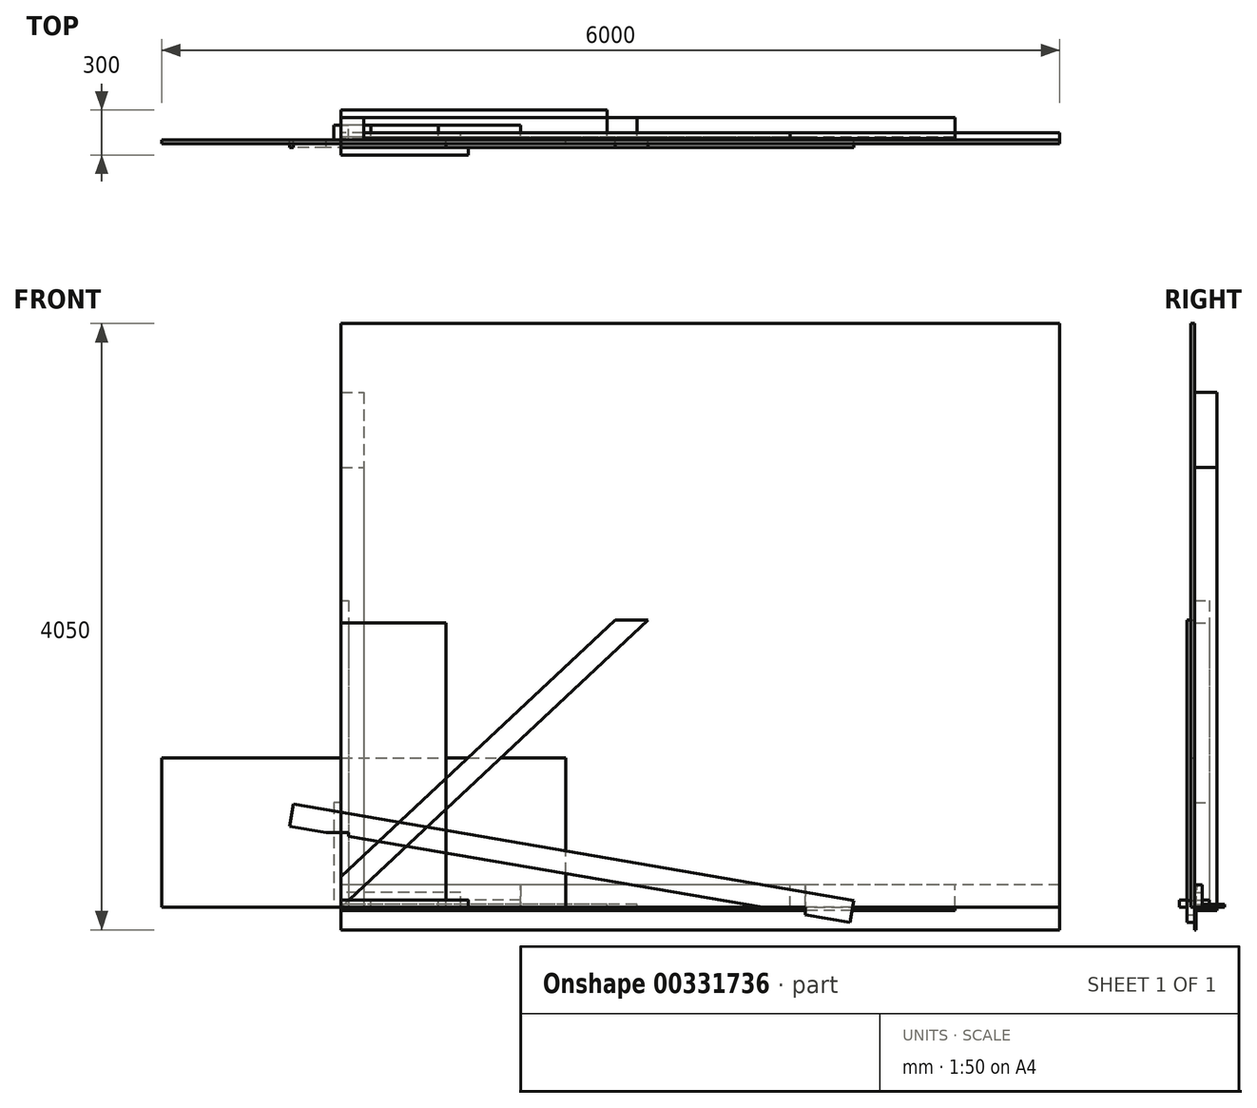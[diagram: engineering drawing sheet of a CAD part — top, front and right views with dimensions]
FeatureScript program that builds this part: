
annotation { "Feature Type Name" : "Feature", "Feature Type Description" : "" }
export const myFeature = defineFeature(function(context is Context, id is Id, definition is map)
    precondition{}
    {
        {
            var Q0;
            Q0=qCreatedBy(makeId("Top.planeOp"),FACE);
            var sketch = newSketch(context, id + "F0", { "sketchPlane" : qUnion([Q0])});
            skLineSegment(sketch, "E0.bottom", {"start": v(0, 0) * mm, "end": v(150, 0) * mm});
            skLineSegment(sketch, "E0.top", {"start": v(0, 150) * mm, "end": v(150, 150) * mm});
            skLineSegment(sketch, "E0.left", {"start": v(0, 0) * mm, "end": v(0, 150) * mm});
            skLineSegment(sketch, "E0.right", {"start": v(150, 0) * mm, "end": v(150, 150) * mm});
            skSolve(sketch);
        }
        {
            var Q0;
            Q0=makeQuery(id+"F0.imprint","IMPRINT",FACE,{"disambiguationData":[TD([[makeQuery(id+"F0.imprint","IMPRINT",EDGE,{"derivedFrom":sQuery(id+"F0.wireOp",EDGE,"E0.bottom")}),1.0]])]});
            extrude(context, id + "F1", {"entities" : qUnion([Q0]), "depth" : 3440 * mm});
        }
        {
            var Q0;
            Q0=qCreatedBy(makeId("Top.planeOp"),FACE);
            var sketch = newSketch(context, id + "F2", { "sketchPlane" : qUnion([Q0])});
            skLineSegment(sketch, "E1.bottom", {"start": v(0, 0) * mm, "end": v(150, 0) * mm});
            skLineSegment(sketch, "E1.top", {"start": v(0, 150) * mm, "end": v(150, 150) * mm});
            skLineSegment(sketch, "E1.left", {"start": v(0, 0) * mm, "end": v(0, 150) * mm});
            skLineSegment(sketch, "E1.right", {"start": v(150, 0) * mm, "end": v(150, 150) * mm});
            skSolve(sketch);
        }
        {
            var Q0;
            Q0=makeQuery(id+"F2.imprint","IMPRINT",FACE,{"disambiguationData":[TD([[makeQuery(id+"F2.imprint","IMPRINT",EDGE,{"derivedFrom":sQuery(id+"F2.wireOp",EDGE,"E1.bottom")}),1.0]])]});
            extrude(context, id + "F3", {"entities" : qUnion([Q0]), "depth" : 2940 * mm});
        }
        {
            var Q0;
            Q0=qCreatedBy(makeId("Right.planeOp"),FACE);
            var sketch = newSketch(context, id + "F4", { "sketchPlane" : qUnion([Q0])});
            skLineSegment(sketch, "E2.bottom", {"start": v(0, 0) * mm, "end": v(50, 0) * mm});
            skLineSegment(sketch, "E2.top", {"start": v(0, 150) * mm, "end": v(50, 150) * mm});
            skLineSegment(sketch, "E2.left", {"start": v(0, 0) * mm, "end": v(0, 150) * mm});
            skLineSegment(sketch, "E2.right", {"start": v(50, 0) * mm, "end": v(50, 150) * mm});
            skSolve(sketch);
        }
        {
            var Q0;
            Q0=makeQuery(id+"F4.imprint","IMPRINT",FACE,{"disambiguationData":[TD([[makeQuery(id+"F4.imprint","IMPRINT",EDGE,{"derivedFrom":sQuery(id+"F4.wireOp",EDGE,"E2.bottom")}),1.0]])]});
            extrude(context, id + "F5", {"entities" : qUnion([Q0]), "depth" : 4100 * mm});
        }
        {
            var Q0;
            Q0=qCreatedBy(makeId("Right.planeOp"),FACE);
            var sketch = newSketch(context, id + "F6", { "sketchPlane" : qUnion([Q0])});
            skLineSegment(sketch, "E3.bottom", {"start": v(0, 0) * mm, "end": v(50, 0) * mm});
            skLineSegment(sketch, "E3.top", {"start": v(0, 150) * mm, "end": v(50, 150) * mm});
            skLineSegment(sketch, "E3.left", {"start": v(0, 0) * mm, "end": v(0, 150) * mm});
            skLineSegment(sketch, "E3.right", {"start": v(50, 0) * mm, "end": v(50, 150) * mm});
            skSolve(sketch);
        }
        {
            var Q0;
            Q0=makeQuery(id+"F6.imprint","IMPRINT",FACE,{"disambiguationData":[TD([[makeQuery(id+"F6.imprint","IMPRINT",EDGE,{"derivedFrom":sQuery(id+"F6.wireOp",EDGE,"E3.bottom")}),1.0]])]});
            extrude(context, id + "F7", {"entities" : qUnion([Q0]), "depth" : 3000 * mm});
        }
        {
            var Q0;
            Q0=qCreatedBy(makeId("Right.planeOp"),FACE);
            var sketch = newSketch(context, id + "F8", { "sketchPlane" : qUnion([Q0])});
            skLineSegment(sketch, "E4.bottom", {"start": v(0, 0) * mm, "end": v(50, 0) * mm});
            skLineSegment(sketch, "E4.top", {"start": v(0, 150) * mm, "end": v(50, 150) * mm});
            skLineSegment(sketch, "E4.left", {"start": v(0, 0) * mm, "end": v(0, 150) * mm});
            skLineSegment(sketch, "E4.right", {"start": v(50, 0) * mm, "end": v(50, 150) * mm});
            skSolve(sketch);
        }
        {
            var Q0;
            Q0=makeQuery(id+"F8.imprint","IMPRINT",FACE,{"disambiguationData":[TD([[makeQuery(id+"F8.imprint","IMPRINT",EDGE,{"derivedFrom":sQuery(id+"F8.wireOp",EDGE,"E4.bottom")}),1.0]])]});
            extrude(context, id + "F9", {"entities" : qUnion([Q0]), "depth" : 4800 * mm});
        }
        {
            var Q0;
            Q0=qCreatedBy(makeId("Right.planeOp"),FACE);
            var sketch = newSketch(context, id + "F10", { "sketchPlane" : qUnion([Q0])});
            skLineSegment(sketch, "E5.bottom", {"start": v(0, 0) * mm, "end": v(150, 0) * mm});
            skLineSegment(sketch, "E5.top", {"start": v(0, -20) * mm, "end": v(150, -20) * mm});
            skLineSegment(sketch, "E5.left", {"start": v(0, 0) * mm, "end": v(0, -20) * mm});
            skLineSegment(sketch, "E5.right", {"start": v(150, 0) * mm, "end": v(150, -20) * mm});
            skSolve(sketch);
        }
        {
            var Q0;
            Q0=makeQuery(id+"F10.imprint","IMPRINT",FACE,{"disambiguationData":[TD([[makeQuery(id+"F10.imprint","IMPRINT",EDGE,{"derivedFrom":sQuery(id+"F10.wireOp",EDGE,"E5.bottom")}),-1.0]])]});
            extrude(context, id + "F11", {"entities" : qUnion([Q0]), "depth" : 4100 * mm});
        }
        {
            var Q0;
            Q0=qCreatedBy(makeId("Right.planeOp"),FACE);
            var sketch = newSketch(context, id + "F12", { "sketchPlane" : qUnion([Q0])});
            skLineSegment(sketch, "E6.bottom", {"start": v(0, 0) * mm, "end": v(200, 0) * mm});
            skLineSegment(sketch, "E6.top", {"start": v(0, 20) * mm, "end": v(200, 20) * mm});
            skLineSegment(sketch, "E6.left", {"start": v(0, 0) * mm, "end": v(0, 20) * mm});
            skLineSegment(sketch, "E6.right", {"start": v(200, 0) * mm, "end": v(200, 20) * mm});
            skSolve(sketch);
        }
        {
            var Q0;
            Q0=makeQuery(id+"F12.imprint","IMPRINT",FACE,{"disambiguationData":[TD([[makeQuery(id+"F12.imprint","IMPRINT",EDGE,{"derivedFrom":sQuery(id+"F12.wireOp",EDGE,"E6.bottom")}),1.0]])]});
            extrude(context, id + "F13", {"entities" : qUnion([Q0]), "depth" : 1775 * mm});
        }
        {
            var Q0;
            Q0=makeQuery(id+"F13.opExtrude","SWEPT_BODY",BODY,{"disambiguationData":[OSD([sQuery(id+"F12.wireOp",EDGE,"E6.bottom"),sQuery(id+"F12.wireOp",EDGE,"E6.top"),sQuery(id+"F12.wireOp",EDGE,"E6.left"),sQuery(id+"F12.wireOp",EDGE,"E6.right")])]});
            transform(context, id + "F14", {"entities" : qUnion([Q0]), "transformType" : TransformType.TRANSLATION_3D, "dx" : 0 * mm, "dy" : 0 * mm, "dz" : 0 * mm, "makeCopy" : true});
        }
        {
            var Q0;
            Q0=makeQuery(id+"F14.opPattern","COPY",BODY,{"derivedFrom":makeQuery(id+"F13.opExtrude","SWEPT_BODY",BODY,{"disambiguationData":[OSD([sQuery(id+"F12.wireOp",EDGE,"E6.bottom"),sQuery(id+"F12.wireOp",EDGE,"E6.top"),sQuery(id+"F12.wireOp",EDGE,"E6.left"),sQuery(id+"F12.wireOp",EDGE,"E6.right")])]}),"instanceName":"1"});
            deleteBodies(context, id + "F15", {"entities" : qUnion([Q0])});
        }
        {
            var Q0;
            Q0=qCreatedBy(makeId("Right.planeOp"),FACE);
            var sketch = newSketch(context, id + "F16", { "sketchPlane" : qUnion([Q0])});
            skLineSegment(sketch, "E7.bottom", {"start": v(0, 0) * mm, "end": v(150, 0) * mm});
            skLineSegment(sketch, "E7.top", {"start": v(0, 20) * mm, "end": v(150, 20) * mm});
            skLineSegment(sketch, "E7.left", {"start": v(0, 0) * mm, "end": v(0, 20) * mm});
            skLineSegment(sketch, "E7.right", {"start": v(150, 0) * mm, "end": v(150, 20) * mm});
            skSolve(sketch);
        }
        {
            var Q0;
            Q0=makeQuery(id+"F16.imprint","IMPRINT",FACE,{"disambiguationData":[TD([[makeQuery(id+"F16.imprint","IMPRINT",EDGE,{"derivedFrom":sQuery(id+"F16.wireOp",EDGE,"E7.bottom")}),1.0]])]});
            extrude(context, id + "F17", {"entities" : qUnion([Q0]), "depth" : 1975 * mm});
        }
        {
            var Q0;
            Q0=qCreatedBy(makeId("Front.planeOp"),FACE);
            var sketch = newSketch(context, id + "F18", { "sketchPlane" : qUnion([Q0])});
            skLineSegment(sketch, "E8", {"start": v(2899.7, 0) * mm, "end": v(3100, 0) * mm});
            skLineSegment(sketch, "E9.bottom", {"start": v(3100, 0) * mm, "end": v(3050, 0) * mm});
            skLineSegment(sketch, "E9.left", {"start": v(3100, 0) * mm, "end": v(3100, -50.14) * mm});
            skPoint(sketch, "E9.top.start.orphan", {"position": v(3100, -100.28) * mm});
            skLineSegment(sketch, "E10.bottom", {"start": v(0, 500) * mm, "end": v(50, 500) * mm});
            skLineSegment(sketch, "E11", {"start": v(3400, -100.28) * mm, "end": v(3100, -48.83) * mm});
            skLineSegment(sketch, "E12", {"start": v(-345.31, 542.07) * mm, "end": v(-319.96, 689.91) * mm});
            skLineSegment(sketch, "E13", {"start": v(-319.96, 689.91) * mm, "end": v(3396.99, 52.43) * mm});
            skLineSegment(sketch, "E14", {"start": v(3400, -100.28) * mm, "end": v(3425.36, 47.56) * mm});
            skLineSegment(sketch, "E15", {"start": v(50, 500) * mm, "end": v(-100, 500) * mm});
            skLineSegment(sketch, "E16.trimOffspring", {"start": v(-100, 500) * mm, "end": v(-345.31, 542.07) * mm});
            skLineSegment(sketch, "E17", {"start": v(50, 500) * mm, "end": v(50, 474.27) * mm});
            skLineSegment(sketch, "E18", {"start": v(3396.99, 52.43) * mm, "end": v(3425.36, 47.56) * mm});
            skLineSegment(sketch, "E19.trimOffspring", {"start": v(2815.3, 0) * mm, "end": v(50, 474.27) * mm});
            skLineSegment(sketch, "E20", {"start": v(2815.3, 0) * mm, "end": v(2899.7, 0) * mm});
            skSolve(sketch);
        }
        {
            var Q0;
            Q0=makeQuery(id+"F18.imprint","IMPRINT",FACE,{"disambiguationData":[TD([[makeQuery(id+"F18.imprint","IMPRINT",EDGE,{"derivedFrom":sQuery(id+"F18.wireOp",EDGE,"E8")}),1.0]])]});
            var Q1;
            Q1=makeQuery(id+"F18.imprint","IMPRINT",FACE,{"disambiguationData":[TD([[makeQuery(id+"F18.imprint","IMPRINT",EDGE,{"derivedFrom":sQuery(id+"F18.wireOp",EDGE,"bUrDLvLb-4mLr-TFN3-gRLU-FU5OS9zngxYN.bottom")}),1.0]])]});
            var Q2;
            {var subQ6=sQuery(id+"F18.wireOp",EDGE,"E11");Q2=makeQuery(id+"F18.imprint","IMPRINT",FACE,{"disambiguationData":[TD([[makeQuery(id+"F18.imprint","IMPRINT",EDGE,{"derivedFrom":subQ6}),-1.0]])]});}
            extrude(context, id + "F19", {"entities" : qUnion([Q0, Q1, Q2]), "depth" : 50 * mm});
        }
        {
            var Q0;
            Q0=qCreatedBy(makeId("Right.planeOp"),FACE);
            var sketch = newSketch(context, id + "F20", { "sketchPlane" : qUnion([Q0])});
            skLineSegment(sketch, "E21", {"start": v(10, 0) * mm, "end": v(0, 0.67) * mm});
            skLineSegment(sketch, "E22", {"start": v(10, 0) * mm, "end": v(20, 149.67) * mm});
            skLineSegment(sketch, "E23", {"start": v(0, 0.67) * mm, "end": v(10, 150.33) * mm});
            skLineSegment(sketch, "E24", {"start": v(10, 150.33) * mm, "end": v(20, 149.67) * mm});
            skSolve(sketch);
        }
        {
            var Q0;
            Q0=makeQuery(id+"F20.imprint","IMPRINT",FACE,{"disambiguationData":[TD([[makeQuery(id+"F20.imprint","IMPRINT",EDGE,{"derivedFrom":sQuery(id+"F20.wireOp",EDGE,"LMVcur3E-Yz55-52iU-IUFZ-F79LfoEMaDzR.bottom")}),1.0]])]});
            var Q1;
            Q1=makeQuery(id+"F20.imprint","IMPRINT",FACE,{"disambiguationData":[TD([[makeQuery(id+"F20.imprint","IMPRINT",EDGE,{"derivedFrom":sQuery(id+"F20.wireOp",EDGE,"E21")}),-1.0]])]});
            extrude(context, id + "F21", {"entities" : qUnion([Q0, Q1]), "offsetDistance" : 25 * mm, "depth" : 4100 * mm});
        }
        {
            var Q0;
            Q0=qCreatedBy(makeId("Right.planeOp"),FACE);
            var sketch = newSketch(context, id + "F22", { "sketchPlane" : qUnion([Q0])});
            skLineSegment(sketch, "E25", {"start": v(10, 0) * mm, "end": v(20, 149.67) * mm});
            skLineSegment(sketch, "E26", {"start": v(20, 149.67) * mm, "end": v(10.02, 150.33) * mm});
            skLineSegment(sketch, "E27", {"start": v(10.02, 150.33) * mm, "end": v(0.02, 0.67) * mm});
            skLineSegment(sketch, "E28", {"start": v(10, 0) * mm, "end": v(0, 0.67) * mm});
            skPoint(sketch, "E29.end.orphan", {"position": v(20, 0) * mm});
            skSolve(sketch);
        }
        {
            var Q0;
            Q0=makeQuery(id+"F22.imprint","IMPRINT",FACE,{"disambiguationData":[TD([[makeQuery(id+"F22.imprint","IMPRINT",EDGE,{"derivedFrom":sQuery(id+"F22.wireOp",EDGE,"6NxRIUup-9Sjc-3iok-JrT3-JITKAmBtOCkV.bottom")}),1.0]])]});
            var Q1;
            {var subQ0=sQuery(id+"F22.wireOp",EDGE,"E25");Q1=makeQuery(id+"F22.imprint","IMPRINT",FACE,{"disambiguationData":[TD([[makeQuery(id+"F22.imprint","IMPRINT",EDGE,{"derivedFrom":subQ0}),1.0]])]});}
            extrude(context, id + "F23", {"entities" : qUnion([Q0, Q1]), "depth" : 3100 * mm});
        }
        {
            var Q0;
            Q0=qCreatedBy(makeId("Front.planeOp"),FACE);
            var sketch = newSketch(context, id + "F24", { "sketchPlane" : qUnion([Q0])});
            skLineSegment(sketch, "E30.bottom", {"start": v(0, 0) * mm, "end": v(4800, 0) * mm});
            skLineSegment(sketch, "E30.top", {"start": v(0, 3900) * mm, "end": v(4800, 3900) * mm});
            skLineSegment(sketch, "E30.left", {"start": v(0, 0) * mm, "end": v(0, 3900) * mm});
            skLineSegment(sketch, "E30.right", {"start": v(4800, 0) * mm, "end": v(4800, 3900) * mm});
            skSolve(sketch);
        }
        {
            var Q0;
            Q0=makeQuery(id+"F24.imprint","IMPRINT",FACE,{"disambiguationData":[TD([[makeQuery(id+"F24.imprint","IMPRINT",EDGE,{"derivedFrom":sQuery(id+"F24.wireOp",EDGE,"E30.bottom")}),1.0]])]});
            extrude(context, id + "F25", {"entities" : qUnion([Q0]), "depth" : 25 * mm});
        }
        {
            var Q0;
            Q0=qCreatedBy(makeId("Front.planeOp"),FACE);
            var sketch = newSketch(context, id + "F26", { "sketchPlane" : qUnion([Q0])});
            skLineSegment(sketch, "E31.bottom", {"start": v(0, 0) * mm, "end": v(700, 0) * mm});
            skLineSegment(sketch, "E31.top", {"start": v(0, 1900) * mm, "end": v(700, 1900) * mm});
            skLineSegment(sketch, "E31.left", {"start": v(0, 0) * mm, "end": v(0, 1900) * mm});
            skLineSegment(sketch, "E31.right", {"start": v(700, 0) * mm, "end": v(700, 1900) * mm});
            skSolve(sketch);
        }
        {
            var Q0;
            Q0=makeQuery(id+"F26.imprint","IMPRINT",FACE,{"disambiguationData":[TD([[makeQuery(id+"F26.imprint","IMPRINT",EDGE,{"derivedFrom":sQuery(id+"F26.wireOp",EDGE,"E31.bottom")}),1.0]])]});
            extrude(context, id + "F27", {"entities" : qUnion([Q0]), "depth" : 50 * mm});
        }
        {
            var Q0;
            Q0=qCreatedBy(makeId("Front.planeOp"),FACE);
            var sketch = newSketch(context, id + "F28", { "sketchPlane" : qUnion([Q0])});
            skLineSegment(sketch, "E32.bottom", {"start": v(0, 0) * mm, "end": v(1500, 0) * mm});
            skLineSegment(sketch, "E32.top", {"start": v(0, 1000) * mm, "end": v(1500, 1000) * mm});
            skLineSegment(sketch, "E32.left", {"start": v(0, 0) * mm, "end": v(0, 1000) * mm});
            skLineSegment(sketch, "E32.right", {"start": v(1500, 0) * mm, "end": v(1500, 1000) * mm});
            skSolve(sketch);
        }
        {
            var Q0;
            Q0=makeQuery(id+"F28.imprint","IMPRINT",FACE,{"disambiguationData":[TD([[makeQuery(id+"F28.imprint","IMPRINT",EDGE,{"derivedFrom":sQuery(id+"F28.wireOp",EDGE,"E32.bottom")}),1.0]])]});
            extrude(context, id + "F29", {"entities" : qUnion([Q0]), "depth" : 25 * mm});
        }
        {
            var Q0;
            Q0=qCreatedBy(makeId("Top.planeOp"),FACE);
            var sketch = newSketch(context, id + "F30", { "sketchPlane" : qUnion([Q0])});
            skLineSegment(sketch, "E33.bottom", {"start": v(0, 0) * mm, "end": v(50, 0) * mm});
            skLineSegment(sketch, "E33.top", {"start": v(0, 100) * mm, "end": v(50, 100) * mm});
            skLineSegment(sketch, "E33.left", {"start": v(0, 0) * mm, "end": v(0, 100) * mm});
            skLineSegment(sketch, "E33.right", {"start": v(50, 0) * mm, "end": v(50, 100) * mm});
            skSolve(sketch);
        }
        {
            var Q0;
            Q0=makeQuery(id+"F30.imprint","IMPRINT",FACE,{"disambiguationData":[TD([[makeQuery(id+"F30.imprint","IMPRINT",EDGE,{"derivedFrom":sQuery(id+"F30.wireOp",EDGE,"E33.bottom")}),1.0]])]});
            extrude(context, id + "F31", {"entities" : qUnion([Q0]), "depth" : 2050 * mm});
        }
        {
            var Q0;
            Q0=qCreatedBy(makeId("Top.planeOp"),FACE);
            var sketch = newSketch(context, id + "F32", { "sketchPlane" : qUnion([Q0])});
            skLineSegment(sketch, "E34.bottom", {"start": v(0, 0) * mm, "end": v(50, 0) * mm});
            skLineSegment(sketch, "E34.top", {"start": v(0, 100) * mm, "end": v(50, 100) * mm});
            skLineSegment(sketch, "E34.left", {"start": v(0, 0) * mm, "end": v(0, 100) * mm});
            skLineSegment(sketch, "E34.right", {"start": v(50, 0) * mm, "end": v(50, 100) * mm});
            skSolve(sketch);
        }
        {
            var Q0;
            Q0=makeQuery(id+"F32.imprint","IMPRINT",FACE,{"disambiguationData":[TD([[makeQuery(id+"F32.imprint","IMPRINT",EDGE,{"derivedFrom":sQuery(id+"F32.wireOp",EDGE,"E34.bottom")}),1.0]])]});
            extrude(context, id + "F33", {"entities" : qUnion([Q0]), "depth" : 1900 * mm});
        }
        {
            var Q0;
            Q0=qCreatedBy(makeId("Right.planeOp"),FACE);
            var sketch = newSketch(context, id + "F34", { "sketchPlane" : qUnion([Q0])});
            skLineSegment(sketch, "E35.bottom", {"start": v(0, 0) * mm, "end": v(50, 0) * mm});
            skLineSegment(sketch, "E35.top", {"start": v(0, 100) * mm, "end": v(50, 100) * mm});
            skLineSegment(sketch, "E35.left", {"start": v(0, 0) * mm, "end": v(0, 100) * mm});
            skLineSegment(sketch, "E35.right", {"start": v(50, 0) * mm, "end": v(50, 100) * mm});
            skSolve(sketch);
        }
        {
            var Q0;
            Q0=makeQuery(id+"F34.imprint","IMPRINT",FACE,{"disambiguationData":[TD([[makeQuery(id+"F34.imprint","IMPRINT",EDGE,{"derivedFrom":sQuery(id+"F34.wireOp",EDGE,"E35.bottom")}),1.0]])]});
            extrude(context, id + "F35", {"entities" : qUnion([Q0]), "depth" : 800 * mm});
        }
        {
            var Q0;
            Q0=qCreatedBy(makeId("Top.planeOp"),FACE);
            var sketch = newSketch(context, id + "F36", { "sketchPlane" : qUnion([Q0])});
            skLineSegment(sketch, "E36.bottom", {"start": v(0, 0) * mm, "end": v(-50, 0) * mm});
            skLineSegment(sketch, "E36.top", {"start": v(0, 100) * mm, "end": v(-50, 100) * mm});
            skLineSegment(sketch, "E36.left", {"start": v(0, 0) * mm, "end": v(0, 100) * mm});
            skLineSegment(sketch, "E36.right", {"start": v(-50, 0) * mm, "end": v(-50, 100) * mm});
            skSolve(sketch);
        }
        {
            var Q0;
            Q0=makeQuery(id+"F36.imprint","IMPRINT",FACE,{"disambiguationData":[TD([[makeQuery(id+"F36.imprint","IMPRINT",EDGE,{"derivedFrom":sQuery(id+"F36.wireOp",EDGE,"E36.bottom")}),-1.0]])]});
            extrude(context, id + "F37", {"entities" : qUnion([Q0]), "depth" : 700 * mm});
        }
        {
            var Q0;
            Q0=qCreatedBy(makeId("Right.planeOp"),FACE);
            var sketch = newSketch(context, id + "F38", { "sketchPlane" : qUnion([Q0])});
            skLineSegment(sketch, "E37.bottom", {"start": v(0, 0) * mm, "end": v(100, 0) * mm});
            skLineSegment(sketch, "E37.top", {"start": v(0, 50) * mm, "end": v(100, 50) * mm});
            skLineSegment(sketch, "E37.left", {"start": v(0, 0) * mm, "end": v(0, 50) * mm});
            skLineSegment(sketch, "E37.right", {"start": v(100, 0) * mm, "end": v(100, 50) * mm});
            skSolve(sketch);
        }
        {
            var Q0;
            Q0 = qSketchRegion(id + "F38", true);
            extrude(context, id + "F39", {"entities" : qUnion([Q0]), "depth" : 1200 * mm});
        }
        {
            var Q0;
            Q0=qCreatedBy(makeId("Right.planeOp"),FACE);
            var sketch = newSketch(context, id + "F40", { "sketchPlane" : qUnion([Q0])});
            skLineSegment(sketch, "E38.bottom", {"start": v(0, 0) * mm, "end": v(100, 0) * mm});
            skLineSegment(sketch, "E38.top", {"start": v(0, 50) * mm, "end": v(100, 50) * mm});
            skLineSegment(sketch, "E38.left", {"start": v(0, 0) * mm, "end": v(0, 50) * mm});
            skLineSegment(sketch, "E38.right", {"start": v(100, 0) * mm, "end": v(100, 50) * mm});
            skSolve(sketch);
        }
        {
            var Q0;
            Q0=makeQuery(id+"F40.imprint","IMPRINT",FACE,{"disambiguationData":[TD([[makeQuery(id+"F40.imprint","IMPRINT",EDGE,{"derivedFrom":sQuery(id+"F40.wireOp",EDGE,"E38.bottom")}),1.0]])]});
            extrude(context, id + "F41", {"entities" : qUnion([Q0]), "depth" : 200 * mm});
        }
        {
            var Q0;
            Q0=qCreatedBy(makeId("Front.planeOp"),FACE);
            var sketch = newSketch(context, id + "F42", { "sketchPlane" : qUnion([Q0])});
            skLineSegment(sketch, "E39.top", {"start": v(1830.57, 1920) * mm, "end": v(2050, 1920) * mm});
            skLineSegment(sketch, "E39.left", {"start": v(0, 0) * mm, "end": v(0, 205.52) * mm});
            skLineSegment(sketch, "E40", {"start": v(2050, 1920) * mm, "end": v(0, 0) * mm});
            skLineSegment(sketch, "E41", {"start": v(0, 205.52) * mm, "end": v(1830.57, 1920) * mm});
            skSolve(sketch);
        }
        {
            var Q0;
            Q0=makeQuery(id+"F42.imprint","IMPRINT",FACE,{"disambiguationData":[TD([[makeQuery(id+"F42.imprint","IMPRINT",EDGE,{"derivedFrom":sQuery(id+"F42.wireOp",EDGE,"E39.top")}),-1.0]])]});
            extrude(context, id + "F43", {"entities" : qUnion([Q0]), "depth" : 50 * mm});
        }
        {
            var Q0;
            Q0=qCreatedBy(makeId("Right.planeOp"),FACE);
            var sketch = newSketch(context, id + "F44", { "sketchPlane" : qUnion([Q0])});
            skLineSegment(sketch, "E42.bottom", {"start": v(0, 0) * mm, "end": v(-100, 0) * mm});
            skLineSegment(sketch, "E42.top", {"start": v(0, 50) * mm, "end": v(-100, 50) * mm});
            skLineSegment(sketch, "E42.left", {"start": v(0, 0) * mm, "end": v(0, 50) * mm});
            skLineSegment(sketch, "E42.right", {"start": v(-100, 0) * mm, "end": v(-100, 50) * mm});
            skSolve(sketch);
        }
        {
            var Q0;
            Q0=makeQuery(id+"F44.imprint","IMPRINT",FACE,{"disambiguationData":[TD([[makeQuery(id+"F44.imprint","IMPRINT",EDGE,{"derivedFrom":sQuery(id+"F44.wireOp",EDGE,"E42.bottom")}),-1.0]])]});
            extrude(context, id + "F45", {"entities" : qUnion([Q0]), "depth" : 850 * mm});
        }
        {
            var Q0;
            Q0=qCreatedBy(makeId("Right.planeOp"),FACE);
            var sketch = newSketch(context, id + "F46", { "sketchPlane" : qUnion([Q0])});
            skLineSegment(sketch, "E43.bottom", {"start": v(0, 0) * mm, "end": v(100, 0) * mm});
            skLineSegment(sketch, "E43.top", {"start": v(0, 50) * mm, "end": v(100, 50) * mm});
            skLineSegment(sketch, "E43.left", {"start": v(0, 0) * mm, "end": v(0, 50) * mm});
            skLineSegment(sketch, "E43.right", {"start": v(100, 0) * mm, "end": v(100, 50) * mm});
            skSolve(sketch);
        }
        {
            var Q0;
            Q0=makeQuery(id+"F46.imprint","IMPRINT",FACE,{"disambiguationData":[TD([[makeQuery(id+"F46.imprint","IMPRINT",EDGE,{"derivedFrom":sQuery(id+"F46.wireOp",EDGE,"E43.bottom")}),1.0]])]});
            extrude(context, id + "F47", {"entities" : qUnion([Q0]), "depth" : 650 * mm});
        }
        {
            var Q0;
            Q0=qCreatedBy(makeId("Right.planeOp"),FACE);
            var sketch = newSketch(context, id + "F48", { "sketchPlane" : qUnion([Q0])});
            skLineSegment(sketch, "E44", {"start": v(10, 0) * mm, "end": v(20, 149.67) * mm});
            skLineSegment(sketch, "E45", {"start": v(20, 149.67) * mm, "end": v(10, 150.33) * mm});
            skLineSegment(sketch, "E46", {"start": v(10, 150.33) * mm, "end": v(0, 0.67) * mm});
            skLineSegment(sketch, "E47", {"start": v(10, 0) * mm, "end": v(0, 0.67) * mm});
            skSolve(sketch);
        }
        {
            var Q0;
            Q0=makeQuery(id+"F48.imprint","IMPRINT",FACE,{"disambiguationData":[TD([[makeQuery(id+"F48.imprint","IMPRINT",EDGE,{"derivedFrom":sQuery(id+"F48.wireOp",EDGE,"E44")}),1.0]])]});
            extrude(context, id + "F49", {"entities" : qUnion([Q0]), "offsetDistance" : 25 * mm, "depth" : 1200 * mm});
        }
        {
            var Q0;
            Q0=qCreatedBy(makeId("Right.planeOp"),FACE);
            var sketch = newSketch(context, id + "F50", { "sketchPlane" : qUnion([Q0])});
            skLineSegment(sketch, "E48.bottom", {"start": v(0, 0) * mm, "end": v(10, 0) * mm});
            skLineSegment(sketch, "E48.top", {"start": v(0, -150) * mm, "end": v(10, -150) * mm});
            skLineSegment(sketch, "E48.left", {"start": v(0, 0) * mm, "end": v(0, -150) * mm});
            skLineSegment(sketch, "E48.right", {"start": v(10, 0) * mm, "end": v(10, -150) * mm});
            skSolve(sketch);
        }
        {
            var Q0;
            Q0=makeQuery(id+"F50.imprint","IMPRINT",FACE,{"disambiguationData":[TD([[makeQuery(id+"F50.imprint","IMPRINT",EDGE,{"derivedFrom":sQuery(id+"F50.wireOp",EDGE,"E48.bottom")}),-1.0]])]});
            extrude(context, id + "F51", {"entities" : qUnion([Q0]), "depth" : 4800 * mm});
        }
        {
            var Q0;
            Q0=qCreatedBy(makeId("Front.planeOp"),FACE);
            var sketch = newSketch(context, id + "F52", { "sketchPlane" : qUnion([Q0])});
            skLineSegment(sketch, "E49.bottom", {"start": v(0, 0) * mm, "end": v(-1200, 0) * mm});
            skLineSegment(sketch, "E49.top", {"start": v(0, 1000) * mm, "end": v(-1200, 1000) * mm});
            skLineSegment(sketch, "E49.left", {"start": v(0, 0) * mm, "end": v(0, 1000) * mm});
            skLineSegment(sketch, "E49.right", {"start": v(-1200, 0) * mm, "end": v(-1200, 1000) * mm});
            skSolve(sketch);
        }
        {
            var Q0;
            Q0=makeQuery(id+"F52.imprint","IMPRINT",FACE,{"disambiguationData":[TD([[makeQuery(id+"F52.imprint","IMPRINT",EDGE,{"derivedFrom":sQuery(id+"F52.wireOp",EDGE,"E49.bottom")}),-1.0]])]});
            extrude(context, id + "F53", {"entities" : qUnion([Q0]), "depth" : 25 * mm, "offsetDistance" : 25 * mm});
        }
    });
